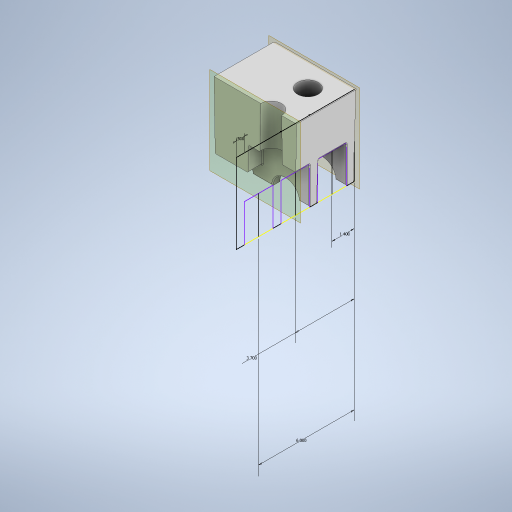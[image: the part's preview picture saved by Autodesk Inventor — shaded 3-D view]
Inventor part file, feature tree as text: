
AUTODESK INVENTOR PART (.ipt)
format: ipt  version: 2023 (Build 270158000, 158)  size: 752,128 bytes
history: native  units: in
note: dims shown in document units (in); Inventor stores cm internally (conversion verified against a paired STEP export)
features: draft x6, extrude x5, sketch x4, fillet x1, plane x1
ambient origin geometry x8: Origin, YZ Plane, XZ Plane, XY Plane, X Axis, Y Axis, Z Axis, Center Point
bodies: Solid1 (feature_tree)
feature tree (17):
  extrude  "Extrusion1"  Depth=5.0in
  sketch  "Sketch2"  dims[d3=7.4in d4=0.0in d6=1.4in]
  extrude  "Extrusion2"  Depth=1.4in
  extrude  "Extrusion3"  Depth=1.5in
  extrude  "Extrusion4"  Depth=0.0625in
  draft  "FaceDraft1"
  draft  "FaceDraft2"
  draft  "FaceDraft3"
  draft  "FaceDraft4"
  draft  "FaceDraft5"
  draft  "FaceDraft6"
  fillet  "Fillet1"  Radius=1.5in
  plane  "Work Plane1"
  extrude  "Extrusion5"  Depth=0.0625in
  sketch  "Sketch1"  dims[d0=5.0in d2=1.625in]
  sketch  "Sketch4"  dims[d7=1.5in d10=1.4in]
  sketch  "Sketch5"  dims[d11=1.5in d13=2.3in d14=1.5in d15=1.4in d16=3.7in d17=6.0in d18=0.5in d20=2.528in d21=7.4in d22=0.0in d23=7.4in d24=0.0in d25=1.5in d26=0.866in d27=1.5in d28=0.0in d29=1.4in d30=5.0in d31=-0.0069in d32=0.0069in d33=0.0069in d34=0.0069in d35=0.0069in d36=0.0069in d37=0.0625in d38=9.0in d39=0.0in]
